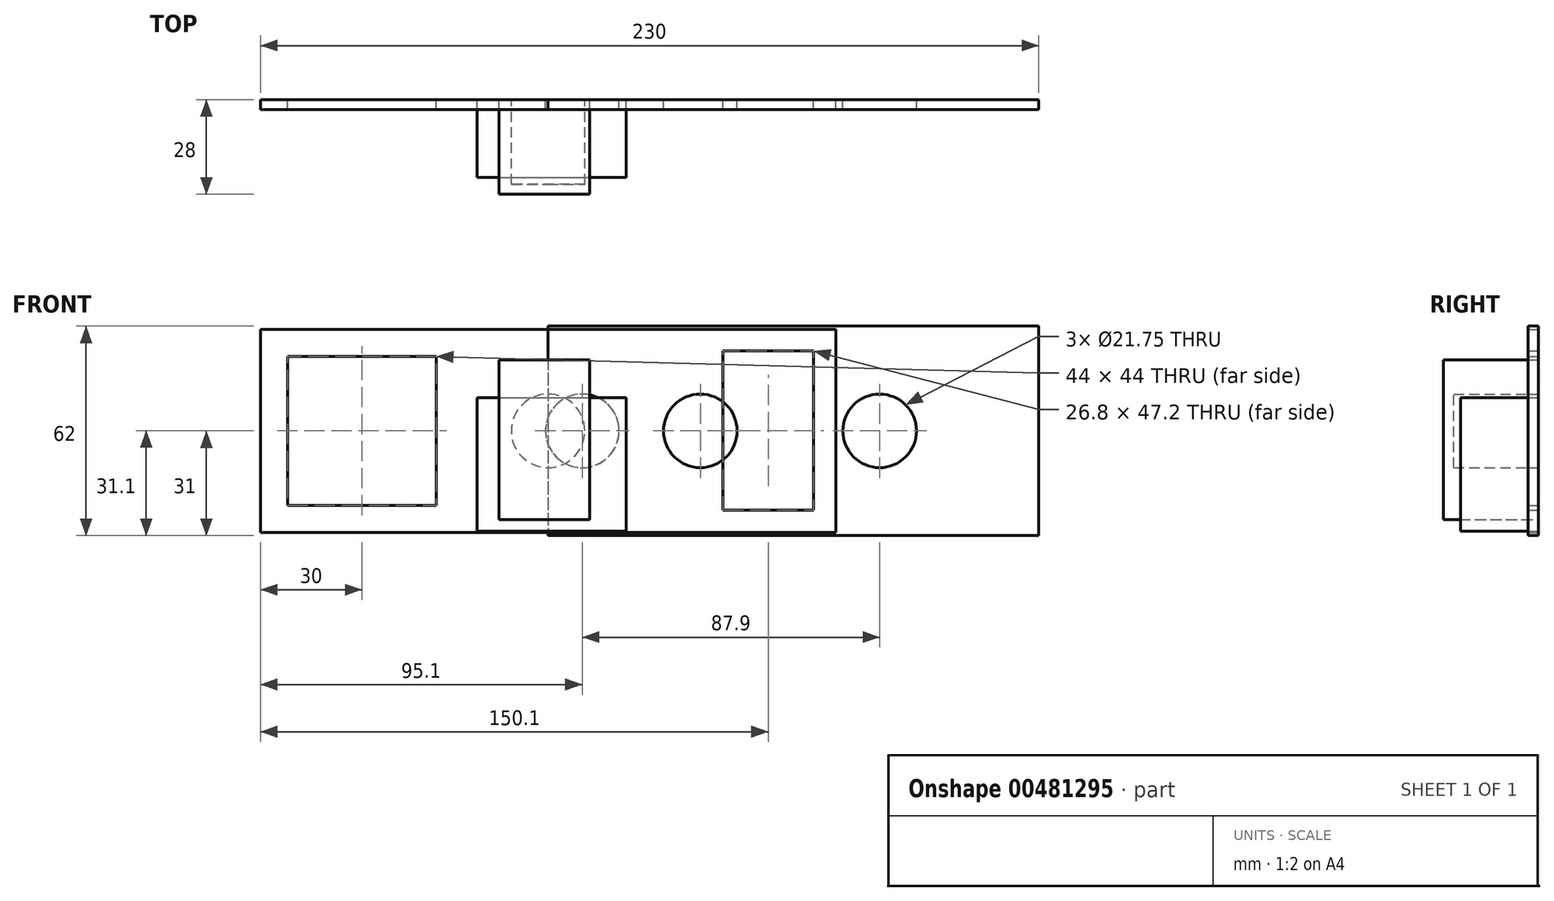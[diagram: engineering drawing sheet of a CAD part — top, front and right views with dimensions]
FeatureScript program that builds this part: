
annotation { "Feature Type Name" : "Feature", "Feature Type Description" : "" }
export const myFeature = defineFeature(function(context is Context, id is Id, definition is map)
    precondition{}
    {
        {
            var Q0;
            Q0=qCreatedBy(makeId("Front.planeOp"),FACE);
            var sketch = newSketch(context, id + "F0", { "sketchPlane" : qUnion([Q0])});
            skLineSegment(sketch, "E0.bottom", {"start": v(-14.5, 20.96) * mm, "end": v(12.3, 20.96) * mm});
            skLineSegment(sketch, "E0.top", {"start": v(-14.5, -26.24) * mm, "end": v(12.3, -26.24) * mm});
            skLineSegment(sketch, "E0.left", {"start": v(-14.5, 20.96) * mm, "end": v(-14.5, -26.24) * mm});
            skLineSegment(sketch, "E0.right", {"start": v(12.3, 20.96) * mm, "end": v(12.3, -26.24) * mm});
            skSolve(sketch);
        }
        {
            var Q0;
            Q0=makeQuery(id+"F0.imprint","IMPRINT",FACE,{"disambiguationData":[TD([[makeQuery(id+"F0.imprint","IMPRINT",EDGE,{"derivedFrom":sQuery(id+"F0.wireOp",EDGE,"E0.bottom")}),-1.0]])]});
            extrude(context, id + "F1", {"entities" : qUnion([Q0]), "depth" : 28 * mm});
        }
        {
            var Q0;
            Q0=qCreatedBy(makeId("Front.planeOp"),FACE);
            var sketch = newSketch(context, id + "F2", { "sketchPlane" : qUnion([Q0])});
            skLineSegment(sketch, "E1.bottom", {"start": v(-20.92, 9.8) * mm, "end": v(23.08, 9.8) * mm});
            skLineSegment(sketch, "E1.top", {"start": v(-20.92, -29.7) * mm, "end": v(23.08, -29.7) * mm});
            skLineSegment(sketch, "E1.left", {"start": v(-20.92, 9.8) * mm, "end": v(-20.92, -29.7) * mm});
            skLineSegment(sketch, "E1.right", {"start": v(23.08, 9.8) * mm, "end": v(23.08, -29.7) * mm});
            skSolve(sketch);
        }
        {
            var Q0;
            Q0 = qSketchRegion(id + "F2", true);
            extrude(context, id + "F3", {"entities" : qUnion([Q0]), "depth" : 23 * mm});
        }
        {
            var Q0;
            Q0=qCreatedBy(makeId("Front.planeOp"),FACE);
            var sketch = newSketch(context, id + "F4", { "sketchPlane" : qUnion([Q0])});
            skCircle(sketch, "E2", {"center": v(0, 0) * mm, "radius": 10.88 * mm});
            skSolve(sketch);
        }
        {
            var Q0;
            Q0 = qSketchRegion(id + "F4", true);
            extrude(context, id + "F5", {"entities" : qUnion([Q0]), "depth" : 25 * mm});
        }
        {
            var Q0;
            Q0=qCreatedBy(makeId("Front.planeOp"),FACE);
            var sketch = newSketch(context, id + "F6", { "sketchPlane" : qUnion([Q0])});
            skLineSegment(sketch, "E3.bottom", {"start": v(0, 31) * mm, "end": v(145, 31) * mm});
            skLineSegment(sketch, "E3.top", {"start": v(0, -31) * mm, "end": v(145, -31) * mm});
            skLineSegment(sketch, "E3.left", {"start": v(0, 31) * mm, "end": v(0, -31) * mm});
            skLineSegment(sketch, "E3.right", {"start": v(145, 31) * mm, "end": v(145, -31) * mm});
            skLineSegment(sketch, "E4", {"start": v(145, 0) * mm, "end": v(0, 0) * mm, "construction": true});
            skLineSegment(sketch, "E5", {"start": v(23, 15) * mm, "end": v(23, -16.3) * mm, "construction": true});
            skLineSegment(sketch, "E6", {"start": v(117, 21.84) * mm, "end": v(117, -17.38) * mm, "construction": true});
            skCircle(sketch, "E7", {"center": v(98, 0) * mm, "radius": 10.88 * mm});
            skLineSegment(sketch, "E8", {"start": v(83, 0) * mm, "end": v(113, 0) * mm, "construction": true});
            skLineSegment(sketch, "E9", {"start": v(98, 20) * mm, "end": v(98, -20) * mm, "construction": true});
            skLineSegment(sketch, "E10", {"start": v(83, 0) * mm, "end": v(83, 20) * mm, "construction": true});
            skLineSegment(sketch, "E11", {"start": v(83, 20) * mm, "end": v(98, 20) * mm, "construction": true});
            skLineSegment(sketch, "E12", {"start": v(98, 20) * mm, "end": v(113, 20) * mm, "construction": true});
            skLineSegment(sketch, "E13", {"start": v(113, 20) * mm, "end": v(113, 0) * mm, "construction": true});
            skLineSegment(sketch, "E14", {"start": v(113, 0) * mm, "end": v(113, -20) * mm, "construction": true});
            skLineSegment(sketch, "E15", {"start": v(113, -20) * mm, "end": v(98, -20) * mm, "construction": true});
            skLineSegment(sketch, "E16", {"start": v(98, -20) * mm, "end": v(83, -20) * mm, "construction": true});
            skLineSegment(sketch, "E17", {"start": v(83, -20) * mm, "end": v(83, 0) * mm, "construction": true});
            skCircle(sketch, "E18", {"center": v(45, 0) * mm, "radius": 10.88 * mm});
            skLineSegment(sketch, "E19", {"start": v(30, 0) * mm, "end": v(60, 0) * mm, "construction": true});
            skLineSegment(sketch, "E20", {"start": v(45, 20) * mm, "end": v(45, -20) * mm, "construction": true});
            skLineSegment(sketch, "E21", {"start": v(30, 0) * mm, "end": v(30, 20) * mm, "construction": true});
            skLineSegment(sketch, "E22", {"start": v(30, 20) * mm, "end": v(45, 20) * mm, "construction": true});
            skLineSegment(sketch, "E23", {"start": v(45, 20) * mm, "end": v(60, 20) * mm, "construction": true});
            skLineSegment(sketch, "E24", {"start": v(60, 20) * mm, "end": v(60, 0) * mm, "construction": true});
            skLineSegment(sketch, "E25", {"start": v(60, 0) * mm, "end": v(60, -20) * mm, "construction": true});
            skLineSegment(sketch, "E26", {"start": v(60, -20) * mm, "end": v(45, -20) * mm, "construction": true});
            skLineSegment(sketch, "E27", {"start": v(45, -20) * mm, "end": v(30, -20) * mm, "construction": true});
            skLineSegment(sketch, "E28", {"start": v(30, -20) * mm, "end": v(30, 0) * mm, "construction": true});
            skSolve(sketch);
        }
        {
            var Q0;
            Q0 = qSketchRegion(id + "F6", true);
            extrude(context, id + "F7", {"entities" : qUnion([Q0]), "depth" : 3 * mm});
        }
        {
            var Q0;
            Q0=qCreatedBy(makeId("Front.planeOp"),FACE);
            var sketch = newSketch(context, id + "F8", { "sketchPlane" : qUnion([Q0])});
            skLineSegment(sketch, "E29", {"start": v(-85, 0) * mm, "end": v(85, 0) * mm, "construction": true});
            skLineSegment(sketch, "E30", {"start": v(-85, 0) * mm, "end": v(-85, 30) * mm});
            skLineSegment(sketch, "E31", {"start": v(-85, 30) * mm, "end": v(85, 30) * mm});
            skLineSegment(sketch, "E32", {"start": v(85, 30) * mm, "end": v(85, 0) * mm});
            skLineSegment(sketch, "E33", {"start": v(85, 0) * mm, "end": v(85, -30) * mm});
            skLineSegment(sketch, "E34", {"start": v(85, -30) * mm, "end": v(-85, -30) * mm});
            skLineSegment(sketch, "E35", {"start": v(-85, -30) * mm, "end": v(-85, 0) * mm});
            skCircle(sketch, "E36", {"center": v(10.1, 0) * mm, "radius": 10.88 * mm});
            skLineSegment(sketch, "E37", {"start": v(-55, 25) * mm, "end": v(-55, -25) * mm, "construction": true});
            skLineSegment(sketch, "E38", {"start": v(-55, -25) * mm, "end": v(-30, -25) * mm, "construction": true});
            skLineSegment(sketch, "E39", {"start": v(-30, -25) * mm, "end": v(-30, 25) * mm, "construction": true});
            skLineSegment(sketch, "E40", {"start": v(-30, 25) * mm, "end": v(-55, 25) * mm, "construction": true});
            skLineSegment(sketch, "E41", {"start": v(-80, 25) * mm, "end": v(-80, -25) * mm, "construction": true});
            skLineSegment(sketch, "E42", {"start": v(-80, -25) * mm, "end": v(-55, -25) * mm, "construction": true});
            skLineSegment(sketch, "E43", {"start": v(-55, 25) * mm, "end": v(-80, 25) * mm, "construction": true});
            skLineSegment(sketch, "E44", {"start": v(65.1, 23.7) * mm, "end": v(65.1, -23.5) * mm, "construction": true});
            skLineSegment(sketch, "E45", {"start": v(65.1, 23.7) * mm, "end": v(78.5, 23.7) * mm});
            skLineSegment(sketch, "E46", {"start": v(78.5, 23.7) * mm, "end": v(78.5, -23.5) * mm});
            skLineSegment(sketch, "E47", {"start": v(78.5, -23.5) * mm, "end": v(65.1, -23.5) * mm});
            skLineSegment(sketch, "E48", {"start": v(51.7, -23.5) * mm, "end": v(51.7, 23.7) * mm});
            skLineSegment(sketch, "E49", {"start": v(51.7, 23.7) * mm, "end": v(65.1, 23.7) * mm});
            skLineSegment(sketch, "E50", {"start": v(65.1, -23.5) * mm, "end": v(51.7, -23.5) * mm});
            skLineSegment(sketch, "E51", {"start": v(80, 25.2) * mm, "end": v(80, -26.84) * mm, "construction": true});
            skLineSegment(sketch, "E52", {"start": v(80, 25.2) * mm, "end": v(50.2, 25.2) * mm, "construction": true});
            skLineSegment(sketch, "E53", {"start": v(50.2, 25.2) * mm, "end": v(50.2, -25) * mm, "construction": true});
            skLineSegment(sketch, "E54", {"start": v(50.2, -25) * mm, "end": v(80, -25) * mm, "construction": true});
            skLineSegment(sketch, "E55", {"start": v(-33, 22) * mm, "end": v(-33, -22) * mm});
            skLineSegment(sketch, "E56", {"start": v(-33, -22) * mm, "end": v(-77, -22) * mm});
            skLineSegment(sketch, "E57", {"start": v(-77, -22) * mm, "end": v(-77, 22) * mm});
            skLineSegment(sketch, "E58", {"start": v(-77, 22) * mm, "end": v(-33, 22) * mm});
            skSolve(sketch);
        }
        {
            var Q0;
            Q0 = qSketchRegion(id + "F8", true);
            extrude(context, id + "F9", {"entities" : qUnion([Q0]), "depth" : 3 * mm});
        }
    });
